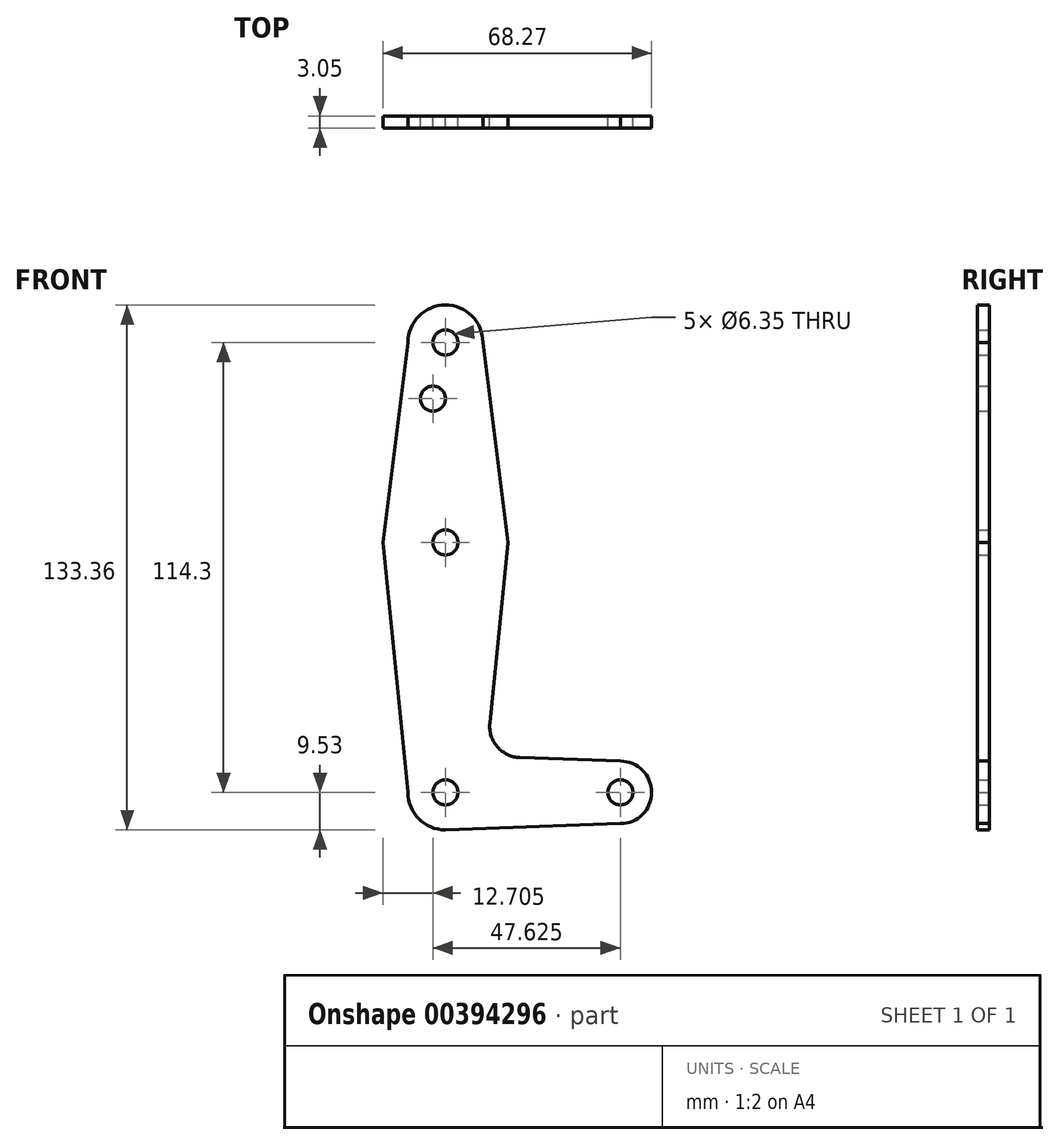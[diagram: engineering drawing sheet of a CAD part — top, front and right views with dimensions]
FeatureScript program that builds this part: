
annotation { "Feature Type Name" : "Feature", "Feature Type Description" : "" }
export const myFeature = defineFeature(function(context is Context, id is Id, definition is map)
    precondition{}
    {
        {
            var Q0;
            Q0=qCreatedBy(makeId("Front.planeOp"),FACE);
            var sketch = newSketch(context, id + "F0", { "sketchPlane" : qUnion([Q0])});
            skCircle(sketch, "E0", {"center": v(0, 0) * mm, "radius": 9.53 * mm});
            skCircle(sketch, "E1", {"center": v(0, 63.5) * mm, "radius": 15.88 * mm});
            skCircle(sketch, "E2", {"center": v(0, 114.3) * mm, "radius": 9.53 * mm});
            skCircle(sketch, "E3", {"center": v(44.45, 0) * mm, "radius": 7.94 * mm});
            skLineSegment(sketch, "E4", {"start": v(0, 114.3) * mm, "end": v(0, 63.5) * mm, "construction": true});
            skLineSegment(sketch, "E5", {"start": v(0, 0) * mm, "end": v(44.45, 0) * mm, "construction": true});
            skLineSegment(sketch, "E6", {"start": v(0, 63.5) * mm, "end": v(0, 0) * mm, "construction": true});
            skLineSegment(sketch, "E7", {"start": v(-9.53, 114.3) * mm, "end": v(-15.88, 63.5) * mm});
            skLineSegment(sketch, "E8", {"start": v(9.52, 114.3) * mm, "end": v(15.87, 63.5) * mm});
            skLineSegment(sketch, "E9", {"start": v(-15.88, 63.5) * mm, "end": v(-9.53, 0) * mm});
            skLineSegment(sketch, "E10", {"start": v(15.87, 63.5) * mm, "end": v(11.28, 17.59) * mm});
            skLineSegment(sketch, "E11", {"start": v(0, -9.53) * mm, "end": v(44.45, -7.94) * mm});
            skLineSegment(sketch, "E12", {"start": v(18.91, 8.85) * mm, "end": v(44.45, 7.94) * mm});
            skCircle(sketch, "E13", {"center": v(0, 114.3) * mm, "radius": 3.18 * mm});
            skCircle(sketch, "E14", {"center": v(-3.17, 100.03) * mm, "radius": 3.18 * mm});
            skCircle(sketch, "E15", {"center": v(0, 63.5) * mm, "radius": 3.18 * mm});
            skCircle(sketch, "E16", {"center": v(0, 0) * mm, "radius": 3.18 * mm});
            skCircle(sketch, "E17", {"center": v(44.45, 0) * mm, "radius": 3.18 * mm});
            skArc(sketch, "E18.filletArc", {"start": v(11.28, 17.59) * mm, "mid": v(13.2, 11.57) * mm, "end": v(18.91, 8.85) * mm});
            skSolve(sketch);
        }
        {
            var Q0;
            Q0=makeQuery(id+"F0.imprint","IMPRINT",FACE,{"disambiguationData":[TD([[makeQuery(id+"F0.imprint","IMPRINT",EDGE,{"derivedFrom":sQuery(id+"F0.wireOp",EDGE,"E13")}),-1.0]])]});
            var Q1;
            Q1=makeQuery(id+"F0.imprint","IMPRINT",FACE,{"disambiguationData":[TD([[makeQuery(id+"F0.imprint","IMPRINT",EDGE,{"derivedFrom":sQuery(id+"F0.wireOp",EDGE,"E14")}),-1.0]])]});
            var Q2;
            Q2=makeQuery(id+"F0.imprint","IMPRINT",FACE,{"disambiguationData":[TD([[makeQuery(id+"F0.imprint","IMPRINT",EDGE,{"derivedFrom":sQuery(id+"F0.wireOp",EDGE,"E15")}),-1.0]])]});
            var Q3;
            {var subQ11=sQuery(id+"F0.wireOp",EDGE,"E12");Q3=makeQuery(id+"F0.imprint","IMPRINT",FACE,{"disambiguationData":[TD([[makeQuery(id+"F0.imprint","IMPRINT",EDGE,{"derivedFrom":subQ11}),-1.0]])]});}
            var Q4;
            Q4=makeQuery(id+"F0.imprint","IMPRINT",FACE,{"disambiguationData":[TD([[makeQuery(id+"F0.imprint","IMPRINT",EDGE,{"derivedFrom":sQuery(id+"F0.wireOp",EDGE,"E16")}),-1.0]])]});
            var Q5;
            Q5=makeQuery(id+"F0.imprint","IMPRINT",FACE,{"disambiguationData":[TD([[makeQuery(id+"F0.imprint","IMPRINT",EDGE,{"derivedFrom":sQuery(id+"F0.wireOp",EDGE,"E17")}),-1.0]])]});
            extrude(context, id + "F1", {"entities" : qUnion([Q0, Q1, Q2, Q3, Q4, Q5]), "depth" : 3.05 * mm});
        }
    });
